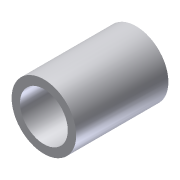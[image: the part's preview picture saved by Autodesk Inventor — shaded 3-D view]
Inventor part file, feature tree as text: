
AUTODESK INVENTOR PART (.ipt)
format: ipt  version: 2011 (Build 150239000, 239)  size: 82,432 bytes
history: native  units: in
note: dims shown in document units (in); Inventor stores cm internally (conversion verified against a paired STEP export)
features: extrude x1, sketch x1
ambient origin geometry x8: Origin, YZ Plane, XZ Plane, XY Plane, X Axis, Y Axis, Z Axis, Center Point
bodies: Solid1 (feature_tree)
feature tree (2):
  extrude  "Extrusion1"  Depth=0.84in
  sketch  "Sketch1"  dims[d0=0.622in d1=0.84in d2=1.2in d3=0.0in]
